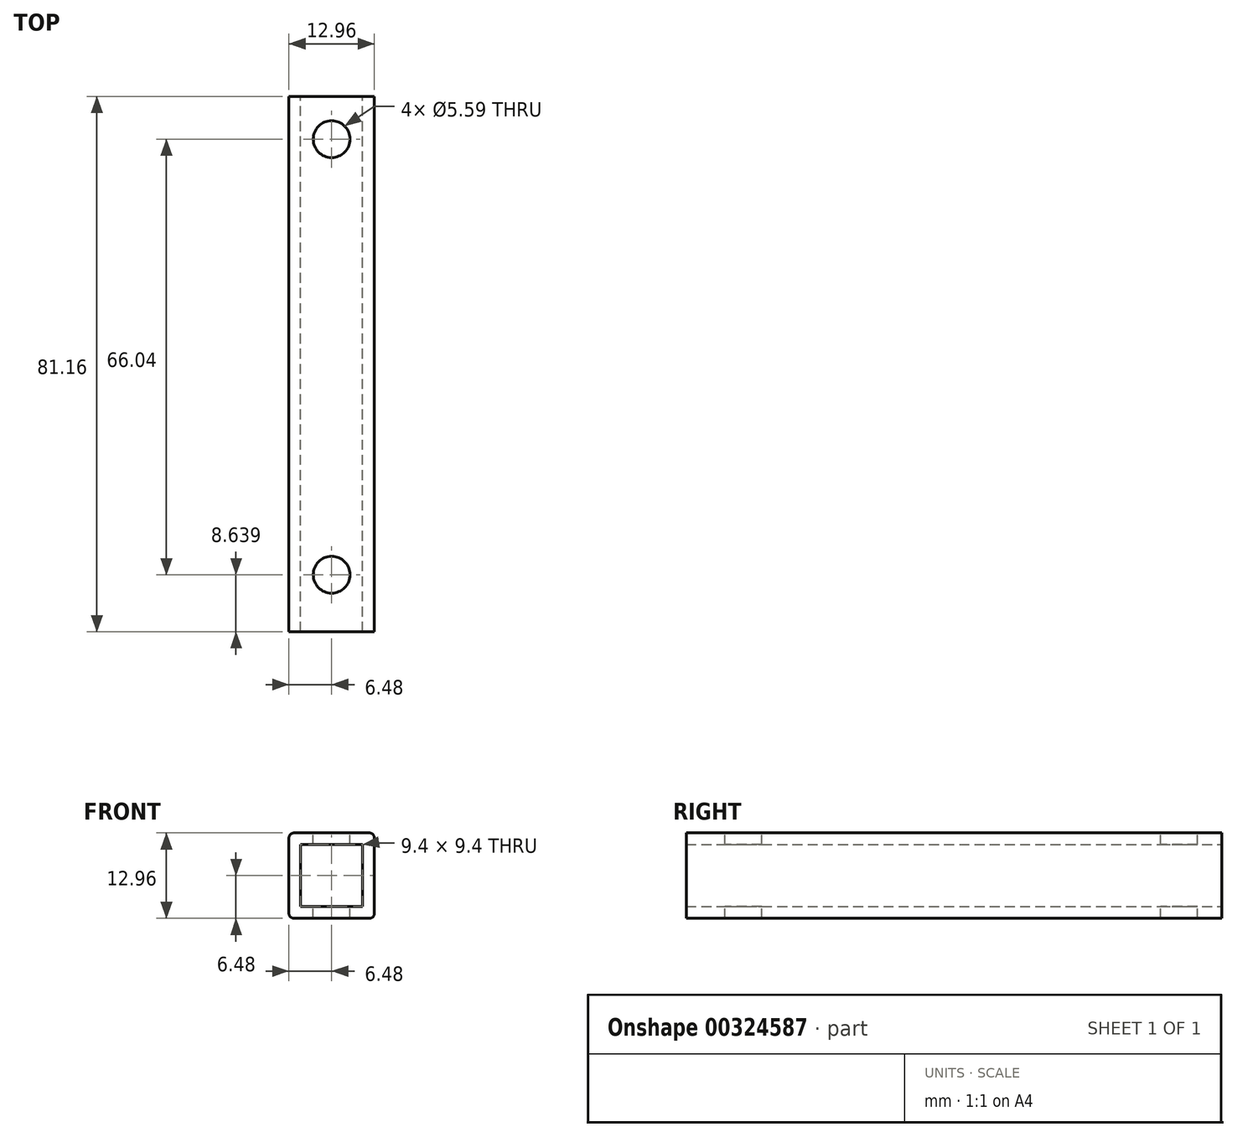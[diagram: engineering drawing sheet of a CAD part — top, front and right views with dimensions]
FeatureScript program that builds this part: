
annotation { "Feature Type Name" : "Feature", "Feature Type Description" : "" }
export const myFeature = defineFeature(function(context is Context, id is Id, definition is map)
    precondition{}
    {
        {
            var Q0;
            Q0=qCreatedBy(makeId("Front.planeOp"),FACE);
            var sketch = newSketch(context, id + "F0", { "sketchPlane" : qUnion([Q0])});
            skLineSegment(sketch, "E0.bottom", {"start": v(-5.72, 6.48) * mm, "end": v(5.72, 6.48) * mm});
            skLineSegment(sketch, "E0.top", {"start": v(-5.72, -6.48) * mm, "end": v(5.72, -6.48) * mm});
            skLineSegment(sketch, "E0.left", {"start": v(-6.48, 5.72) * mm, "end": v(-6.48, -5.71) * mm});
            skLineSegment(sketch, "E0.right", {"start": v(6.48, 5.72) * mm, "end": v(6.48, -5.72) * mm});
            skArc(sketch, "E1.filletArc", {"start": v(-5.72, 6.48) * mm, "mid": v(-6.25, 6.25) * mm, "end": v(-6.48, 5.72) * mm});
            skArc(sketch, "E2.filletArc", {"start": v(6.48, 5.72) * mm, "mid": v(6.25, 6.25) * mm, "end": v(5.72, 6.48) * mm});
            skArc(sketch, "E3.filletArc", {"start": v(5.72, -6.48) * mm, "mid": v(6.25, -6.25) * mm, "end": v(6.48, -5.72) * mm});
            skArc(sketch, "E4.filletArc", {"start": v(-6.48, -5.71) * mm, "mid": v(-6.25, -6.25) * mm, "end": v(-5.72, -6.48) * mm});
            skPoint(sketch, "E5", {"position": v(0, 6.48) * mm});
            skPoint(sketch, "E6", {"position": v(6.48, 0) * mm});
            skLineSegment(sketch, "E7.bottom", {"start": v(-4.7, 4.7) * mm, "end": v(4.7, 4.7) * mm});
            skLineSegment(sketch, "E7.top", {"start": v(-4.7, -4.7) * mm, "end": v(4.7, -4.7) * mm});
            skLineSegment(sketch, "E7.left", {"start": v(-4.7, 4.7) * mm, "end": v(-4.7, -4.7) * mm});
            skLineSegment(sketch, "E7.right", {"start": v(4.7, 4.7) * mm, "end": v(4.7, -4.7) * mm});
            skPoint(sketch, "E8", {"position": v(0, 4.7) * mm});
            skPoint(sketch, "E9", {"position": v(4.7, 0) * mm});
            skSolve(sketch);
        }
        {
            var Q0;
            Q0=makeQuery(id+"F0.imprint","IMPRINT",FACE,{"disambiguationData":[TD([[makeQuery(id+"F0.imprint","IMPRINT",EDGE,{"derivedFrom":sQuery(id+"F0.wireOp",EDGE,"E0.bottom")}),-1.0]])]});
            extrude(context, id + "F1", {"entities" : qUnion([Q0]), "endBound" : BoundingType.SYMMETRIC, "depth" : 81.15 * mm});
        }
        {
            var Q0;
            Q0=makeQuery(id+"F1.opExtrude","SWEPT_FACE",FACE,{"disambiguationData":[OSD([sQuery(id+"F0.wireOp",EDGE,"E0.bottom")])]});
            var sketch = newSketch(context, id + "F2", { "sketchPlane" : qUnion([Q0])});
            skCircle(sketch, "E10", {"center": v(0, -31.94) * mm, "radius": 2.8 * mm});
            skCircle(sketch, "E11", {"center": v(0, 34.1) * mm, "radius": 2.8 * mm});
            skLineSegment(sketch, "E12", {"start": v(0, -31.94) * mm, "end": v(0, 34.1) * mm, "construction": true});
            skPoint(sketch, "E13", {"position": v(0, 1.08) * mm});
            skSolve(sketch);
        }
        {
            var Q0;
            Q0=makeQuery(id+"F2.imprint","IMPRINT",FACE,{"disambiguationData":[TD([[makeQuery(id+"F2.imprint","IMPRINT",EDGE,{"derivedFrom":sQuery(id+"F2.wireOp",EDGE,"E10")}),1.0]])]});
            var Q1;
            Q1=makeQuery(id+"F2.imprint","IMPRINT",FACE,{"disambiguationData":[TD([[makeQuery(id+"F2.imprint","IMPRINT",EDGE,{"derivedFrom":sQuery(id+"F2.wireOp",EDGE,"E11")}),1.0]])]});
            extrude(context, id + "F3", {"entities" : qUnion([Q0, Q1]), "operationType" : NewBodyOperationType.REMOVE, "endBound" : BoundingType.THROUGH_ALL, "oppositeDirection" : true, "depth" : 25.4 * mm});
        }
        {
            var Q0;
            Q0=sQuery(id+"F2.wireOp",EDGE,"E12");
            cPoint(context, id + "F4", {"entities" : qUnion([Q0]), "parameter" : 0.5});
        }
        {
            var Q0;
            Q0 = qCreatedBy(id + "F4" ,VERTEX);
            var Q1;
            Q1=qCreatedBy(makeId("Front.planeOp"),FACE);
            cPlane(context, id + "F5", {"entities" : qUnion([Q0, Q1]), "cplaneType" : CPlaneType.PLANE_POINT, "offset" : 25.4 * mm, "width" : 152.4 * mm, "height" : 152.4 * mm});
        }
        {
            var Q0;
            Q0=makeQuery(id+"F1.opExtrude","SWEPT_FACE",FACE,{"disambiguationData":[OSD([sQuery(id+"F0.wireOp",EDGE,"E0.top")])]});
            var sketch = newSketch(context, id + "F6", { "sketchPlane" : qUnion([Q0])});
            skPoint(sketch, "E14", {"position": v(0, -1.08) * mm});
            skSolve(sketch);
        }
    });
